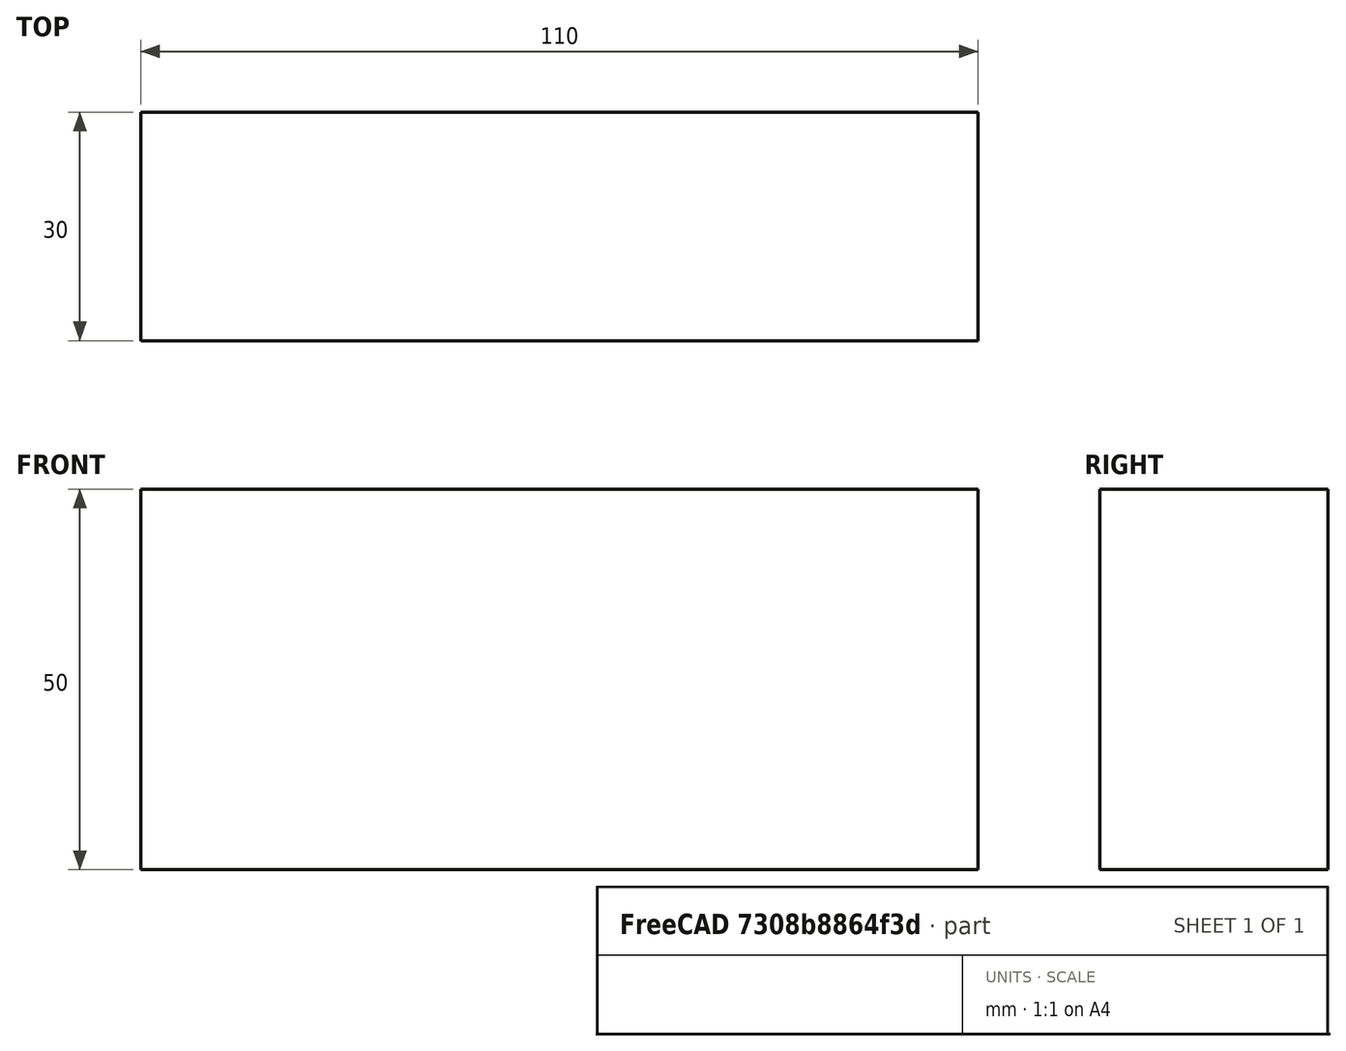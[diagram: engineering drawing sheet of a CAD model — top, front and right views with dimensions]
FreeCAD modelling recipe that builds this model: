
FCSTD DOCUMENT  (FreeCAD 0.15R4671 (Git))
Label: Flat Bar 110x30 EN10058 S235JR
License: All rights reserved
LicenseURL: http://en.wikipedia.org/wiki/All_rights_reserved
objects: Sketcher::SketchObject×1, Part::Extrusion×1
note: 2 computed .brp shape members not serialized (recipe doc carries the construction recipe); baked Part::Feature solids carry a one-line shape summary decoded from their .brp

FEATURE [Sketcher::SketchObject] Sketch
  sketch-geometry (4):
    g0: LineSegment StartX=-55 StartY=-15 StartZ=0 EndX=55 EndY=-15 EndZ=0
    g1: LineSegment StartX=55 StartY=-15 StartZ=0 EndX=55 EndY=15 EndZ=0
    g2: LineSegment StartX=55 StartY=15 StartZ=0 EndX=-55 EndY=15 EndZ=0
    g3: LineSegment StartX=-55 StartY=15 StartZ=0 EndX=-55 EndY=-15 EndZ=0
  constraints (12):
    c: Coincident(g0,g1)
    c: Coincident(g1,g2)
    c: Coincident(g2,g3)
    c: Coincident(g3,g0)
    c: Horizontal(g0)
    c: Horizontal(g2)
    c: Vertical(g1)
    c: Vertical(g3)
    c: Symmetric(g1,g2,g-2)
    c: Symmetric(g0,g1,g-1)
    c: DistanceY(g1) = 30
    c: DistanceX(g0) = 110
FEATURE [Part::Extrusion] Extrude  label="Flat Bar 110x30 EN10058 S235JR"
  Base = -> Sketch
  Dir = (0,0,50)
  Solid = true
